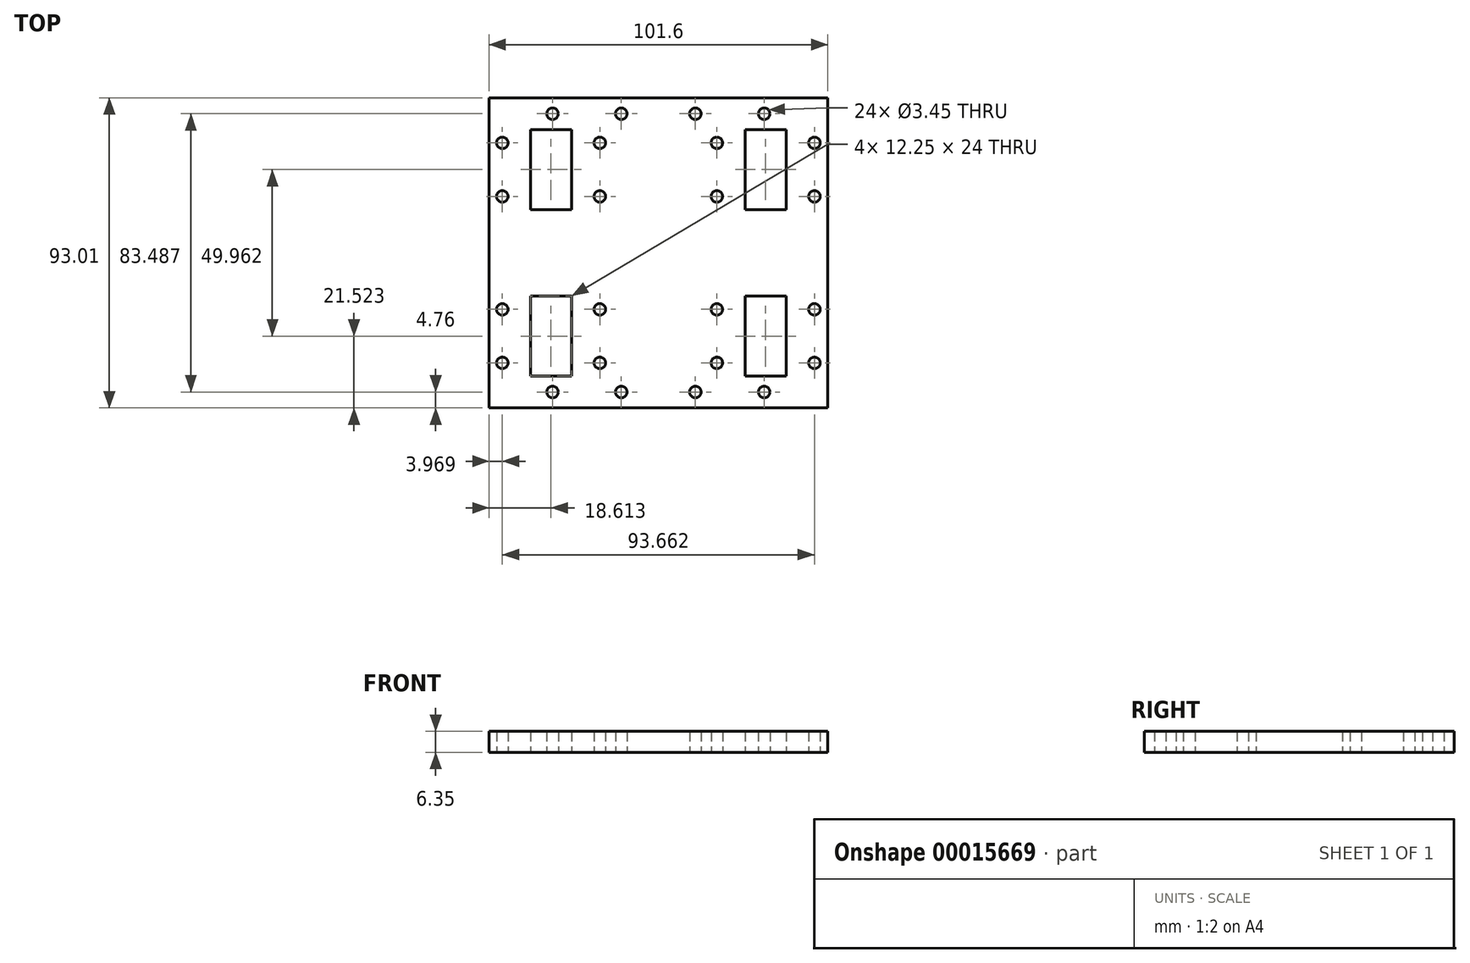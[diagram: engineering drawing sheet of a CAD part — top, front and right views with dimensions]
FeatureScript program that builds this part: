
annotation { "Feature Type Name" : "Feature", "Feature Type Description" : "" }
export const myFeature = defineFeature(function(context is Context, id is Id, definition is map)
    precondition{}
    {
        {
            var Q0;
            Q0=qCreatedBy(makeId("Top.planeOp"),FACE);
            var sketch = newSketch(context, id + "F0", { "sketchPlane" : qUnion([Q0])});
            skLineSegment(sketch, "E0.bottom", {"start": v(0, 0) * mm, "end": v(101.6, 0) * mm});
            skLineSegment(sketch, "E0.top", {"start": v(0, -93.01) * mm, "end": v(101.6, -93.01) * mm});
            skLineSegment(sketch, "E0.left", {"start": v(0, 0) * mm, "end": v(0, -93.01) * mm});
            skLineSegment(sketch, "E0.right", {"start": v(101.6, 0) * mm, "end": v(101.6, -93.01) * mm});
            skLineSegment(sketch, "E1.bottom", {"start": v(76.86, -9.53) * mm, "end": v(89.11, -9.53) * mm});
            skLineSegment(sketch, "E1.top", {"start": v(76.86, -33.53) * mm, "end": v(89.11, -33.53) * mm});
            skLineSegment(sketch, "E1.left", {"start": v(76.86, -9.53) * mm, "end": v(76.86, -33.53) * mm});
            skLineSegment(sketch, "E1.right", {"start": v(89.11, -9.53) * mm, "end": v(89.11, -33.53) * mm});
            skLineSegment(sketch, "E2.bottom", {"start": v(76.86, -59.49) * mm, "end": v(89.11, -59.49) * mm});
            skLineSegment(sketch, "E2.top", {"start": v(76.86, -83.49) * mm, "end": v(89.11, -83.49) * mm});
            skLineSegment(sketch, "E2.left", {"start": v(76.86, -59.49) * mm, "end": v(76.86, -83.49) * mm});
            skLineSegment(sketch, "E2.right", {"start": v(89.11, -59.49) * mm, "end": v(89.11, -83.49) * mm});
            skLineSegment(sketch, "E3", {"start": v(89.11, -83.49) * mm, "end": v(97.63, -83.49) * mm, "construction": true});
            skLineSegment(sketch, "E4", {"start": v(97.63, -83.49) * mm, "end": v(97.63, -79.52) * mm, "construction": true});
            skLineSegment(sketch, "E5", {"start": v(89.11, -59.49) * mm, "end": v(97.63, -59.49) * mm, "construction": true});
            skLineSegment(sketch, "E6", {"start": v(97.63, -59.49) * mm, "end": v(97.63, -63.46) * mm, "construction": true});
            skLineSegment(sketch, "E7", {"start": v(76.86, -59.49) * mm, "end": v(68.34, -59.49) * mm, "construction": true});
            skLineSegment(sketch, "E8", {"start": v(68.34, -59.49) * mm, "end": v(68.34, -63.46) * mm, "construction": true});
            skLineSegment(sketch, "E9", {"start": v(76.86, -83.49) * mm, "end": v(68.34, -83.49) * mm, "construction": true});
            skLineSegment(sketch, "E10", {"start": v(68.34, -83.49) * mm, "end": v(68.34, -79.52) * mm, "construction": true});
            skLineSegment(sketch, "E11", {"start": v(76.86, -9.53) * mm, "end": v(68.34, -9.53) * mm, "construction": true});
            skLineSegment(sketch, "E12", {"start": v(68.34, -9.53) * mm, "end": v(68.34, -13.5) * mm, "construction": true});
            skLineSegment(sketch, "E13", {"start": v(76.86, -33.53) * mm, "end": v(68.34, -33.53) * mm, "construction": true});
            skLineSegment(sketch, "E14", {"start": v(68.34, -33.53) * mm, "end": v(68.34, -29.56) * mm, "construction": true});
            skLineSegment(sketch, "E15", {"start": v(89.11, -33.53) * mm, "end": v(97.63, -33.53) * mm, "construction": true});
            skLineSegment(sketch, "E16", {"start": v(97.63, -33.53) * mm, "end": v(97.63, -29.56) * mm, "construction": true});
            skLineSegment(sketch, "E17", {"start": v(89.11, -9.53) * mm, "end": v(97.63, -9.53) * mm, "construction": true});
            skLineSegment(sketch, "E18", {"start": v(97.63, -9.53) * mm, "end": v(97.63, -13.5) * mm, "construction": true});
            skCircle(sketch, "E19", {"center": v(97.63, -13.5) * mm, "radius": 1.73 * mm});
            skCircle(sketch, "E20", {"center": v(97.63, -29.56) * mm, "radius": 1.73 * mm});
            skCircle(sketch, "E21", {"center": v(68.34, -29.56) * mm, "radius": 1.73 * mm});
            skCircle(sketch, "E22", {"center": v(68.34, -13.5) * mm, "radius": 1.73 * mm});
            skCircle(sketch, "E23", {"center": v(68.34, -63.46) * mm, "radius": 1.73 * mm});
            skCircle(sketch, "E24", {"center": v(97.63, -63.46) * mm, "radius": 1.73 * mm});
            skCircle(sketch, "E25", {"center": v(97.63, -79.52) * mm, "radius": 1.73 * mm});
            skCircle(sketch, "E26", {"center": v(68.34, -79.52) * mm, "radius": 1.73 * mm});
            skLineSegment(sketch, "E27", {"start": v(97.63, -63.46) * mm, "end": v(101.6, -63.46) * mm});
            skLineSegment(sketch, "E28", {"start": v(3.97, -9.53) * mm, "end": v(3.97, -13.5) * mm});
            skLineSegment(sketch, "E29", {"start": v(3.97, -9.53) * mm, "end": v(12.49, -9.53) * mm, "construction": true});
            skLineSegment(sketch, "E30", {"start": v(24.74, -9.53) * mm, "end": v(33.26, -9.53) * mm, "construction": true});
            skLineSegment(sketch, "E31", {"start": v(33.26, -9.52) * mm, "end": v(33.26, -13.5) * mm});
            skLineSegment(sketch, "E32.bottom", {"start": v(12.49, -9.53) * mm, "end": v(24.74, -9.53) * mm});
            skLineSegment(sketch, "E32.top", {"start": v(12.49, -33.52) * mm, "end": v(24.74, -33.52) * mm});
            skLineSegment(sketch, "E32.left", {"start": v(12.49, -9.53) * mm, "end": v(12.49, -33.53) * mm});
            skLineSegment(sketch, "E32.right", {"start": v(24.74, -9.53) * mm, "end": v(24.74, -33.52) * mm});
            skLineSegment(sketch, "E33", {"start": v(24.74, -33.52) * mm, "end": v(33.26, -33.52) * mm, "construction": true});
            skLineSegment(sketch, "E34", {"start": v(12.49, -33.52) * mm, "end": v(3.97, -33.52) * mm, "construction": true});
            skLineSegment(sketch, "E35", {"start": v(3.97, -33.53) * mm, "end": v(3.97, -29.56) * mm});
            skLineSegment(sketch, "E36", {"start": v(33.26, -33.53) * mm, "end": v(33.26, -29.56) * mm});
            skLineSegment(sketch, "E37.bottom", {"start": v(12.49, -59.49) * mm, "end": v(24.74, -59.49) * mm});
            skLineSegment(sketch, "E37.top", {"start": v(12.49, -83.49) * mm, "end": v(24.74, -83.49) * mm});
            skLineSegment(sketch, "E37.left", {"start": v(12.49, -59.49) * mm, "end": v(12.49, -83.49) * mm});
            skLineSegment(sketch, "E37.right", {"start": v(24.74, -59.49) * mm, "end": v(24.74, -83.49) * mm});
            skLineSegment(sketch, "E38", {"start": v(12.49, -59.49) * mm, "end": v(3.97, -59.49) * mm, "construction": true});
            skLineSegment(sketch, "E39", {"start": v(3.97, -59.49) * mm, "end": v(3.97, -63.46) * mm, "construction": true});
            skLineSegment(sketch, "E40", {"start": v(24.74, -59.49) * mm, "end": v(33.26, -59.49) * mm, "construction": true});
            skLineSegment(sketch, "E41", {"start": v(33.26, -59.49) * mm, "end": v(33.26, -63.46) * mm, "construction": true});
            skLineSegment(sketch, "E42", {"start": v(24.74, -83.49) * mm, "end": v(33.26, -83.49) * mm, "construction": true});
            skLineSegment(sketch, "E43", {"start": v(33.26, -83.49) * mm, "end": v(33.26, -79.52) * mm, "construction": true});
            skLineSegment(sketch, "E44", {"start": v(12.49, -83.49) * mm, "end": v(3.97, -83.49) * mm, "construction": true});
            skLineSegment(sketch, "E45", {"start": v(3.97, -83.49) * mm, "end": v(3.97, -79.52) * mm, "construction": true});
            skCircle(sketch, "E46", {"center": v(3.97, -63.46) * mm, "radius": 1.73 * mm});
            skCircle(sketch, "E47", {"center": v(33.26, -63.46) * mm, "radius": 1.73 * mm});
            skCircle(sketch, "E48", {"center": v(33.26, -79.52) * mm, "radius": 1.73 * mm});
            skCircle(sketch, "E49", {"center": v(3.97, -79.52) * mm, "radius": 1.73 * mm});
            skCircle(sketch, "E50", {"center": v(33.26, -13.5) * mm, "radius": 1.73 * mm});
            skCircle(sketch, "E51", {"center": v(33.26, -29.56) * mm, "radius": 1.73 * mm});
            skCircle(sketch, "E52", {"center": v(3.97, -29.56) * mm, "radius": 1.73 * mm});
            skCircle(sketch, "E53", {"center": v(3.97, -13.5) * mm, "radius": 1.73 * mm});
            skLineSegment(sketch, "E54", {"start": v(101.6, -88.25) * mm, "end": v(82.55, -88.25) * mm});
            skLineSegment(sketch, "E55", {"start": v(82.55, -88.25) * mm, "end": v(61.91, -88.25) * mm, "construction": true});
            skLineSegment(sketch, "E56", {"start": v(61.91, -88.25) * mm, "end": v(39.69, -88.25) * mm});
            skLineSegment(sketch, "E57", {"start": v(39.69, -88.25) * mm, "end": v(19.05, -88.25) * mm, "construction": true});
            skLineSegment(sketch, "E58", {"start": v(19.05, -88.25) * mm, "end": v(0, -88.25) * mm, "construction": true});
            skLineSegment(sketch, "E59", {"start": v(101.6, -4.76) * mm, "end": v(82.55, -4.76) * mm, "construction": true});
            skLineSegment(sketch, "E60", {"start": v(82.55, -4.76) * mm, "end": v(61.91, -4.76) * mm, "construction": true});
            skLineSegment(sketch, "E61", {"start": v(61.91, -4.76) * mm, "end": v(39.69, -4.76) * mm});
            skLineSegment(sketch, "E62", {"start": v(39.69, -4.76) * mm, "end": v(19.05, -4.76) * mm, "construction": true});
            skLineSegment(sketch, "E63", {"start": v(19.05, -4.76) * mm, "end": v(0, -4.76) * mm, "construction": true});
            skCircle(sketch, "E64", {"center": v(19.05, -88.25) * mm, "radius": 1.73 * mm});
            skCircle(sketch, "E65", {"center": v(39.69, -88.25) * mm, "radius": 1.73 * mm});
            skCircle(sketch, "E66", {"center": v(39.69, -4.76) * mm, "radius": 1.73 * mm});
            skCircle(sketch, "E67", {"center": v(19.05, -4.76) * mm, "radius": 1.73 * mm});
            skCircle(sketch, "E68", {"center": v(61.91, -4.76) * mm, "radius": 1.73 * mm});
            skCircle(sketch, "E69", {"center": v(82.55, -4.76) * mm, "radius": 1.73 * mm});
            skCircle(sketch, "E70", {"center": v(82.55, -88.25) * mm, "radius": 1.73 * mm});
            skCircle(sketch, "E71", {"center": v(61.91, -88.25) * mm, "radius": 1.73 * mm});
            skLineSegment(sketch, "E72", {"start": v(50.8, -4.76) * mm, "end": v(50.8, 0) * mm});
            skLineSegment(sketch, "E73", {"start": v(50.8, -88.25) * mm, "end": v(50.8, -93.01) * mm});
            skLineSegment(sketch, "E74", {"start": v(18.61, -33.53) * mm, "end": v(18.61, -59.49) * mm});
            skLineSegment(sketch, "E75", {"start": v(82.99, -33.53) * mm, "end": v(82.99, -59.49) * mm});
            skLineSegment(sketch, "E76", {"start": v(18.61, -46.5) * mm, "end": v(0, -46.5) * mm});
            skLineSegment(sketch, "E77", {"start": v(82.99, -46.5) * mm, "end": v(101.6, -46.5) * mm});
            skLineSegment(sketch, "E78", {"start": v(19.05, -4.76) * mm, "end": v(19.05, -9.53) * mm});
            skSolve(sketch);
        }
        {
            var Q0;
            Q0 = qSketchRegion(id + "F0", true);
            extrude(context, id + "F1", {"entities" : qUnion([Q0]), "depth" : 6.35 * mm});
        }
    });
